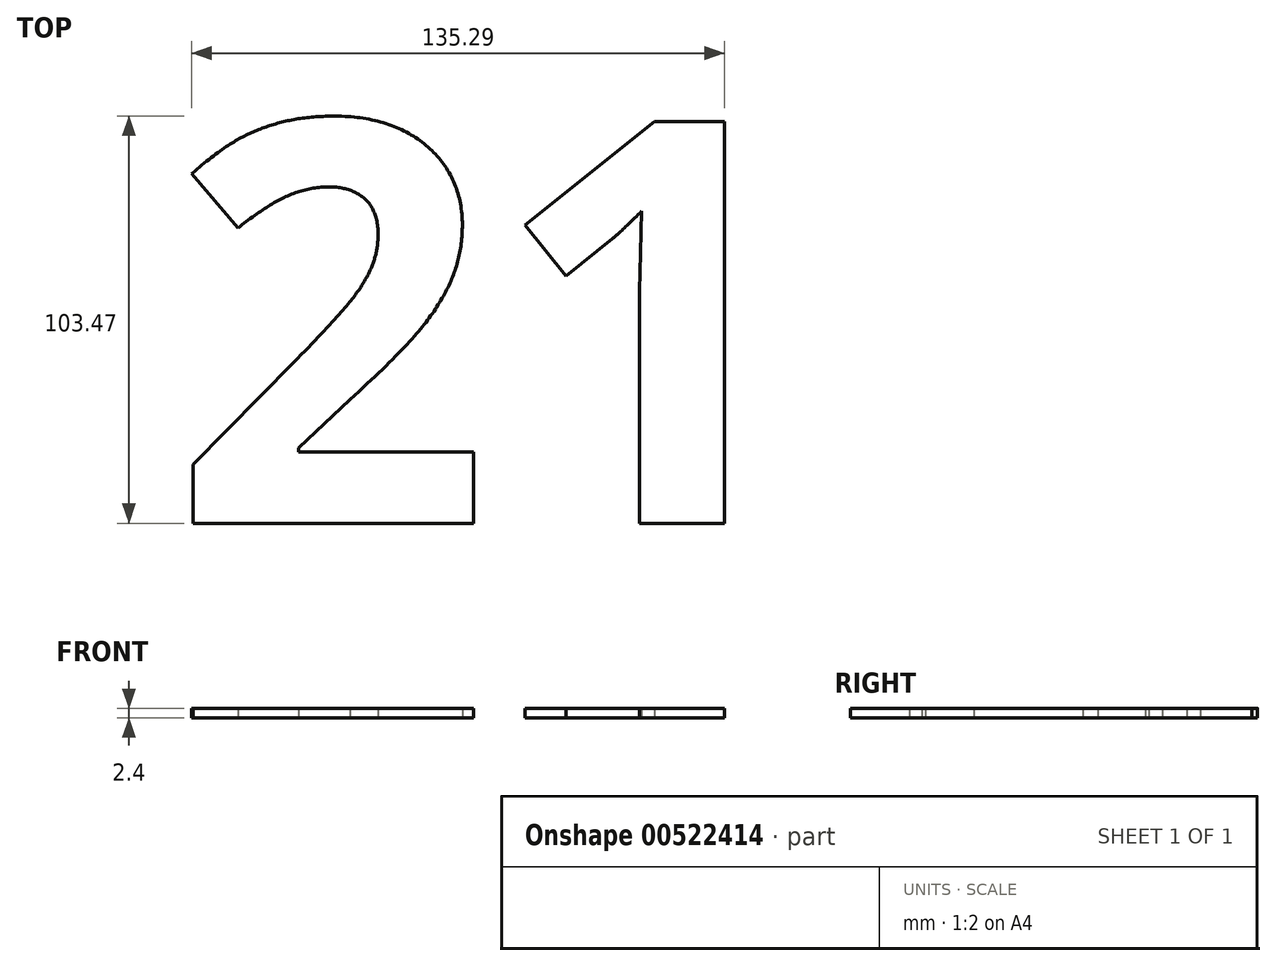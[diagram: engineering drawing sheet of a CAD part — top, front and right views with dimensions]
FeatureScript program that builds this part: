
annotation { "Feature Type Name" : "Feature", "Feature Type Description" : "" }
export const myFeature = defineFeature(function(context is Context, id is Id, definition is map)
    precondition{}
    {
        {
            var Q0;
            Q0=qCreatedBy(makeId("Top.planeOp"),FACE);
            var sketch = newSketch(context, id + "F0", { "sketchPlane" : qUnion([Q0])});
            skText(sketch, "E0", { "text": "21", "fontName": "NotoSans-Bold.ttf"});
            const initialGuessF0  = {"E0": [-0.0745, -0.04349, 1, 0, 0.10289]};
            skSetInitialGuess(sketch, initialGuessF0);
            skSolve(sketch);
        }
        {
            var Q0;
            Q0=makeQuery(id+"F0.imprint","IMPRINT",FACE,{"disambiguationData":[TD([[makeQuery(id+"F0.imprint","IMPRINT",EDGE,{"derivedFrom":sQuery(id+"F0.wireOp",EDGE,"E0.sketch_text.stroke-0")}),-1.0]])]});
            var Q1;
            Q1=makeQuery(id+"F0.imprint","IMPRINT",FACE,{"disambiguationData":[TD([[makeQuery(id+"F0.imprint","IMPRINT",EDGE,{"derivedFrom":sQuery(id+"F0.wireOp",EDGE,"E0.sketch_text.stroke-24")}),-1.0]])]});
            extrude(context, id + "F1", {"entities" : qUnion([Q0, Q1]), "depth" : 2.4 * mm, "offsetDistance" : 25 * mm});
        }
    });
